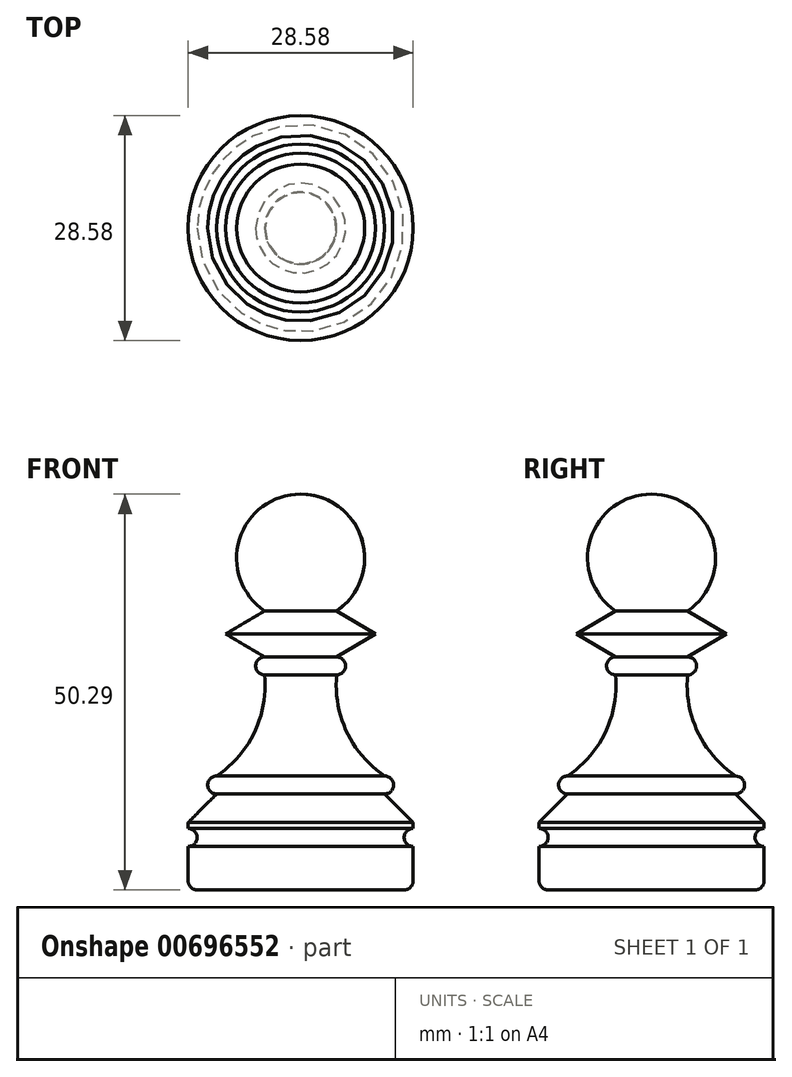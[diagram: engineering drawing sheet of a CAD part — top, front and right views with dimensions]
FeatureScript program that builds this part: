
annotation { "Feature Type Name" : "Feature", "Feature Type Description" : "" }
export const myFeature = defineFeature(function(context is Context, id is Id, definition is map)
    precondition{}
    {
        {
            var Q0;
            Q0=qCreatedBy(makeId("Front.planeOp"),FACE);
            var sketch = newSketch(context, id + "F0", { "sketchPlane" : qUnion([Q0])});
            skLineSegment(sketch, "E0", {"start": v(0, 0) * mm, "end": v(10.67, 0) * mm});
            skLineSegment(sketch, "E1", {"start": v(10.67, 0) * mm, "end": v(14.29, -3.62) * mm});
            skLineSegment(sketch, "E2", {"start": v(14.29, -3.62) * mm, "end": v(14.29, -4.38) * mm});
            skArc(sketch, "E3", {"start": v(14.29, -4.38) * mm, "mid": v(13.14, -5.52) * mm, "end": v(14.29, -6.67) * mm});
            skLineSegment(sketch, "E4", {"start": v(14.29, -6.67) * mm, "end": v(14.29, -12.2) * mm});
            skLineSegment(sketch, "E5", {"start": v(14.29, -12.2) * mm, "end": v(0, -12.2) * mm});
            skLineSegment(sketch, "E6", {"start": v(0, -12.2) * mm, "end": v(0, 0) * mm});
            skSolve(sketch);
        }
        {
            var Q0;
            Q0=makeQuery(id+"F0.imprint","IMPRINT",FACE,{"disambiguationData":[TD([[makeQuery(id+"F0.imprint","IMPRINT",EDGE,{"derivedFrom":sQuery(id+"F0.wireOp",EDGE,"E0")}),-1.0]])]});
            var Q1;
            Q1=sQuery(id+"F0.wireOp",EDGE,"E6");
            revolve(context, id + "F1", {"entities" : qUnion([Q0]), "axis" : qUnion([Q1]), "revolveType" : RevolveType.FULL});
        }
        {
            var Q0;
            Q0=makeQuery(id+"F1.opRevolve","SWEPT_EDGE",EDGE,{"disambiguationData":[OSD([sQuery(id+"F0.wireOp",EDGE,"E4"),sQuery(id+"F0.wireOp",EDGE,"E5")])]});
            fillet(context, id + "F2", {"entities" : qUnion([Q0]), "radius" : 1.14 * mm, "tangentPropagation" : true, "allowEdgeOverflow" : false});
        }
        {
            var Q0;
            Q0=qCreatedBy(makeId("Front.planeOp"),FACE);
            var sketch = newSketch(context, id + "F3", { "sketchPlane" : qUnion([Q0])});
            skLineSegment(sketch, "E7", {"start": v(10.67, 0) * mm, "end": v(0, 0) * mm});
            skLineSegment(sketch, "E8", {"start": v(0, 0) * mm, "end": v(0, 38.1) * mm});
            skArc(sketch, "E9", {"start": v(4.57, 23.25) * mm, "mid": v(7.77, 32.36) * mm, "end": v(0, 38.1) * mm});
            skLineSegment(sketch, "E10", {"start": v(4.57, 23.25) * mm, "end": v(9.53, 20.33) * mm});
            skLineSegment(sketch, "E11", {"start": v(9.53, 20.33) * mm, "end": v(4.57, 17.4) * mm});
            skArc(sketch, "E12", {"start": v(4.57, 15.12) * mm, "mid": v(5.72, 16.27) * mm, "end": v(4.57, 17.4) * mm});
            skArc(sketch, "E13", {"start": v(4.57, 15.12) * mm, "mid": v(5.87, 7.87) * mm, "end": v(10.67, 2.29) * mm});
            skArc(sketch, "E14", {"start": v(10.67, 0) * mm, "mid": v(11.81, 1.14) * mm, "end": v(10.67, 2.29) * mm});
            skSolve(sketch);
        }
        {
            var Q0;
            Q0=qSketchRegion(id+"F3",true);
            var Q1;
            Q1=sQuery(id+"F3.wireOp",EDGE,"E8");
            revolve(context, id + "F4", {"operationType" : NewBodyOperationType.ADD, "entities" : qUnion([Q0]), "axis" : qUnion([Q1]), "revolveType" : RevolveType.FULL});
        }
    });
